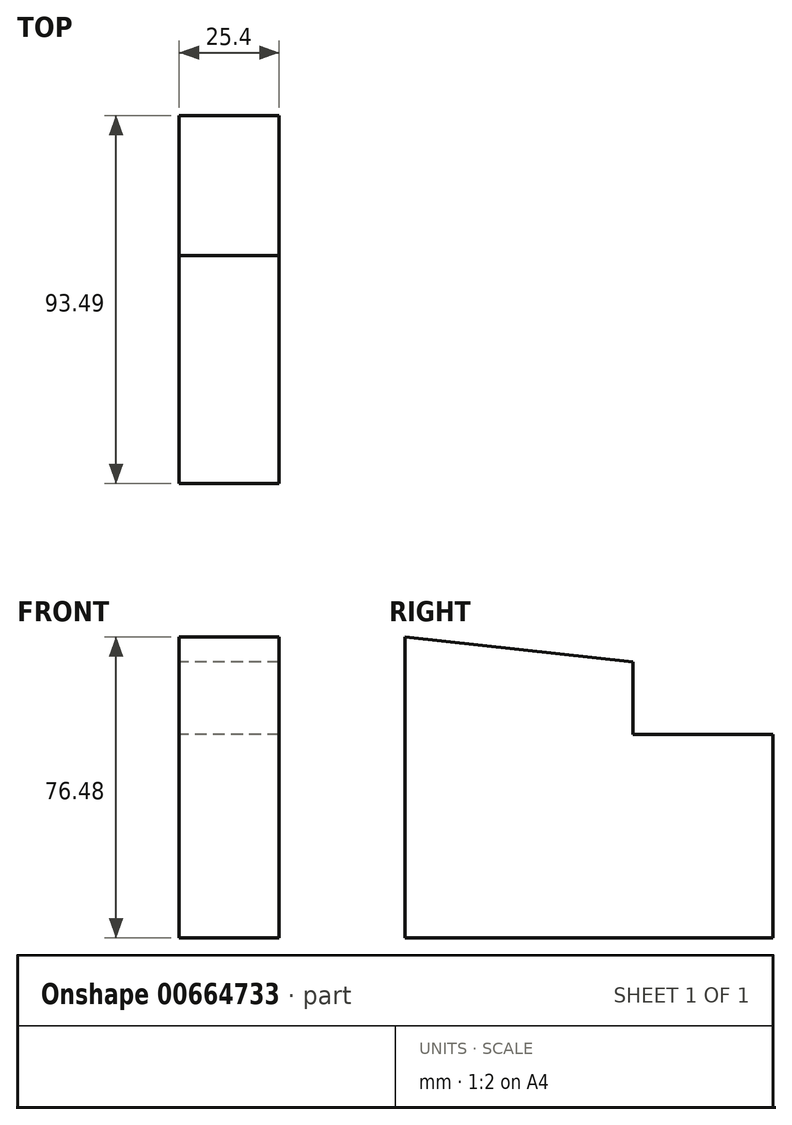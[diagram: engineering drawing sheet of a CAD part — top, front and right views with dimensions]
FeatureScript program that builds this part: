
annotation { "Feature Type Name" : "Feature", "Feature Type Description" : "" }
export const myFeature = defineFeature(function(context is Context, id is Id, definition is map)
    precondition{}
    {
        {
            var Q0;
            Q0=qCreatedBy(makeId("Right.planeOp"),FACE);
            var sketch = newSketch(context, id + "F0", { "sketchPlane" : qUnion([Q0])});
            skLineSegment(sketch, "E0", {"start": v(-39.29, 6.33) * mm, "end": v(-39.29, -70.15) * mm});
            skLineSegment(sketch, "E1", {"start": v(-39.29, -70.15) * mm, "end": v(54.2, -70.15) * mm});
            skLineSegment(sketch, "E2", {"start": v(54.2, -70.15) * mm, "end": v(54.2, -18.47) * mm});
            skLineSegment(sketch, "E3", {"start": v(54.2, -18.47) * mm, "end": v(18.59, -18.47) * mm});
            skLineSegment(sketch, "E4", {"start": v(18.59, -18.47) * mm, "end": v(18.59, 0) * mm});
            skLineSegment(sketch, "E5", {"start": v(18.59, 0) * mm, "end": v(-39.29, 6.33) * mm});
            skSolve(sketch);
        }
        {
            var Q0;
            Q0=makeQuery(id+"F0.imprint","IMPRINT",FACE,{"disambiguationData":[TD([[makeQuery(id+"F0.imprint","IMPRINT",EDGE,{"derivedFrom":sQuery(id+"F0.wireOp",EDGE,"E0")}),1.0]])]});
            extrude(context, id + "F1", {"entities" : qUnion([Q0]), "depth" : 25.4 * mm, "offsetDistance" : 25.4 * mm});
        }
    });
